# Revit family: Lynx - Armchair & Settee
name_source: partatom
category: Furniture
revit_build: Autodesk Revit 2014 (Build: 20130308_1515(x64)
units: mm (PartAtom-declared; Revit-internal decimal feet)

## types (6) — shared parameters
CatURL = http://www.knightsbridge-furniture.co.uk
Dim 2 (D) = 800 mm  [stored 2.62467 ft]
Dim 3 (H) = 760 mm
Finish & Fabrics = http://www.knightsbridge-furniture.co.uk
Manufacturer = Knightsbridge Furniture Productions Ltd.
Product Range = Tubs Clubs and Upholstered Seating
Type Comments = Modern collection of armchairs, 2 and 3 seater sofas
URL = http://www.knightsbridge-furniture.co.uk

## per-type parameters (varying)
| type | 2 seater | 3 Seater | Armchair | CatRef | Description | Dim 1 (W) | Model |
| LYNXK2401 - Lynx Armchair-730w x 800d x 760mm High | No | No | Yes | LYNXK2401 | Lynx Fully Upholstrered Armchair | 730 mm  [stored 2.39501 ft] | Lynx Armchair |
| LYNXK2402 - Lynx 2 Seater Settee-1280w x 800d x 760mm High | Yes | No | No | LYNXK2402 | Lynx Fully Upholstrered Two Seater Settee | 1280 mm  [stored 4.19948 ft] | Lynx 2 Seater Settee |
| LYNXK2403 - Lynx 3 Seater Settee-1930w x 800d x 760mm High | No | Yes | No | LYNXK2403 | Lynx Fully Upholstrered Three Seater Settee | 1930 mm  [stored 6.33202 ft] | Lynx 3 Seater Settee |
| LYNXK2401X - Lynx Armchair - Extreme-730w x 800d x 760mm High | No | No | Yes | LYNXK2401X | Lynx Fully Upholstrered Armchair - Extreme | 730 mm  [stored 2.39501 ft] | Lynx Armchair - Extreme |
| LYNXK2402X - Lynx 2 Seater Settee - Extreme-1280w x 800d x 760mm High | Yes | No | No | LYNXK2402X | Lynx Fully Upholstrered Two Seater Settee - Extreme | 1280 mm  [stored 4.19948 ft] | Lynx 2 Seater Settee - Extreme |
| LYNXK2403X - Lynx 3 Seater Settee - Extreme-1930w x 800d x 760mm High | No | Yes | No | LYNXK2403X | Lynx Fully Upholstrered Three Seater Settee - Extreme | 1930 mm  [stored 6.33202 ft] | Lynx 3 Seater Settee - Extreme |

note: [stored X ft] marks values corroborated as IEEE doubles in the binary element streams (Revit-internal decimal feet)

## geometry (parser evidence)
native form markers: Sweep x15
no freeform markers — native parametric forms only
